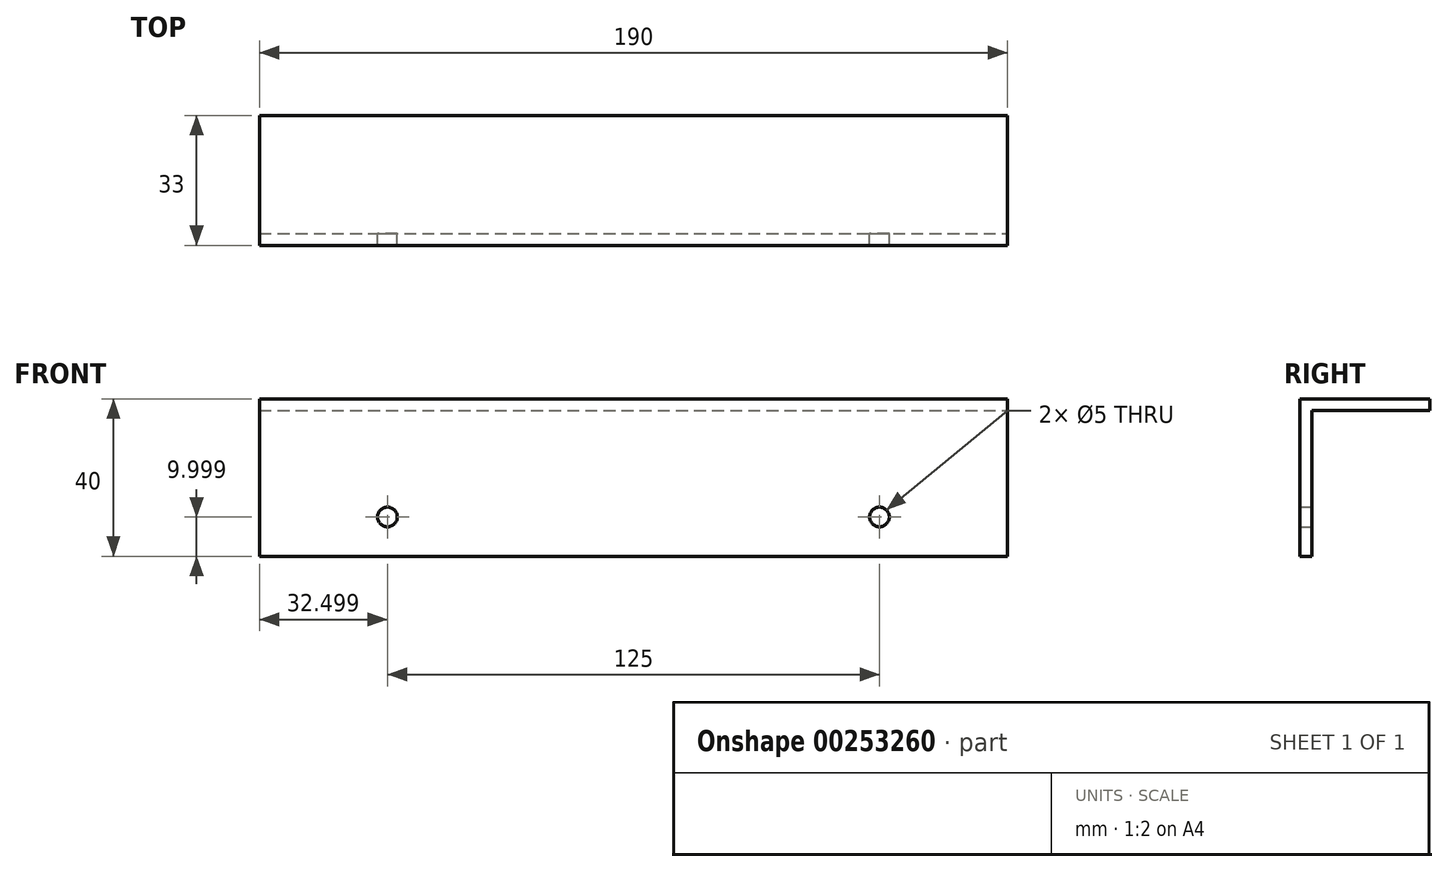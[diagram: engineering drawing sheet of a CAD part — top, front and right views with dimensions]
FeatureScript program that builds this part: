
annotation { "Feature Type Name" : "Feature", "Feature Type Description" : "" }
export const myFeature = defineFeature(function(context is Context, id is Id, definition is map)
    precondition{}
    {
        {
            var Q0;
            Q0=qCreatedBy(makeId("Front.planeOp"),FACE);
            var sketch = newSketch(context, id + "F0", { "sketchPlane" : qUnion([Q0])});
            skLineSegment(sketch, "E0.bottom", {"start": v(-122.06, 41.82) * mm, "end": v(67.94, 41.82) * mm});
            skLineSegment(sketch, "E0.top", {"start": v(-122.06, 1.82) * mm, "end": v(67.94, 1.82) * mm});
            skLineSegment(sketch, "E0.left", {"start": v(-122.06, 41.82) * mm, "end": v(-122.06, 1.82) * mm});
            skLineSegment(sketch, "E0.right", {"start": v(67.94, 41.82) * mm, "end": v(67.94, 1.82) * mm});
            skCircle(sketch, "E1", {"center": v(-89.56, 11.82) * mm, "radius": 2.5 * mm});
            skCircle(sketch, "E2", {"center": v(35.44, 11.82) * mm, "radius": 2.5 * mm});
            skSolve(sketch);
        }
        {
            var Q0;
            Q0=makeQuery(id+"F0.imprint","IMPRINT",FACE,{"disambiguationData":[TD([[makeQuery(id+"F0.imprint","IMPRINT",EDGE,{"derivedFrom":sQuery(id+"F0.wireOp",EDGE,"E0.bottom")}),-1.0]])]});
            extrude(context, id + "F1", {"entities" : qUnion([Q0]), "depth" : 3 * mm});
        }
        {
            var Q0;
            Q0=makeQuery(id+"F1.opExtrude","SWEPT_FACE",FACE,{"disambiguationData":[OSD([sQuery(id+"F0.wireOp",EDGE,"E0.right")])]});
            var sketch = newSketch(context, id + "F2", { "sketchPlane" : qUnion([Q0])});
            skLineSegment(sketch, "E3.bottom", {"start": v(0, 41.82) * mm, "end": v(30, 41.82) * mm});
            skLineSegment(sketch, "E3.top", {"start": v(0, 38.82) * mm, "end": v(30, 38.82) * mm});
            skLineSegment(sketch, "E3.left", {"start": v(0, 41.82) * mm, "end": v(0, 38.82) * mm});
            skLineSegment(sketch, "E3.right", {"start": v(30, 41.82) * mm, "end": v(30, 38.82) * mm});
            skSolve(sketch);
        }
        {
            var Q0;
            Q0 = qSketchRegion(id + "F2", true);
            var Q1;
            Q1=makeQuery(id+"F1.opExtrude","SWEPT_FACE",FACE,{"disambiguationData":[OSD([sQuery(id+"F0.wireOp",EDGE,"E0.left")])]});
            extrude(context, id + "F3", {"entities" : qUnion([Q0]), "operationType" : NewBodyOperationType.ADD, "endBound" : BoundingType.UP_TO_SURFACE, "oppositeDirection" : true, "endBoundEntityFace" : qUnion([Q1]), "depth" : 25 * mm});
        }
    });
